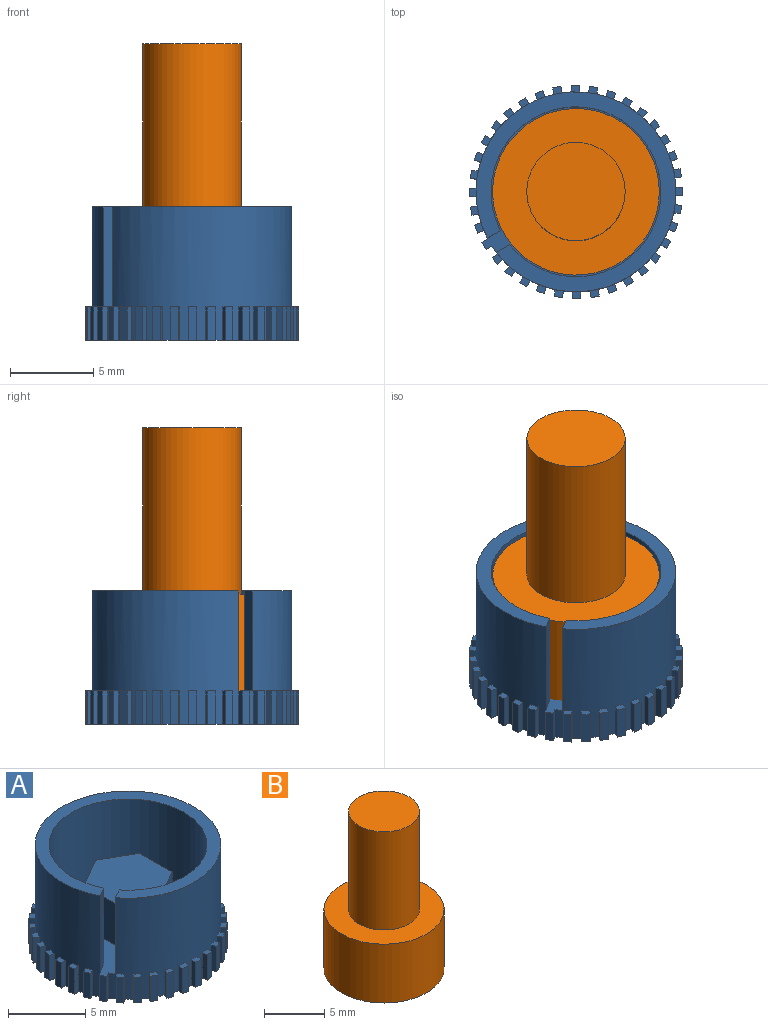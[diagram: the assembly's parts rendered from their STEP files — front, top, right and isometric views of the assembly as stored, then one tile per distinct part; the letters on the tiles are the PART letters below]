
ASSEMBLY  parts=2 mates=1
PART A: 157 faces, bbox 12.8x12.8x8 mm
  f0: plane 3.3x2.55mm, normal (-0.5,-0.87,0), area 9.7mm2, adj f1,f5,f6,f131
  f1: plane 3.3x2.94mm, normal (-1,0,0), area 9.7mm2, adj f0,f2,f6,f131
  f2: plane 3.3x2.55mm, normal (-0.5,0.86,0), area 9.7mm2, adj f1,f3,f6,f131
  f3: plane 3.3x2.55mm, normal (0.5,0.87,0), area 9.7mm2, adj f2,f4,f6,f131
  f4: plane 3.3x2.94mm, normal (1,0,0), area 9.7mm2, adj f3,f5,f6,f131
  f5: plane 3.3x2.55mm, normal (0.5,-0.86,0), area 9.7mm2, adj f0,f4,f6,f131
  f6: plane 5.89x5.11mm, normal (0,0,1), area 22.5mm2, adj f0,f1,f2,f3,f4,f5
  f7: cylinder r=5.1mm len=10.2mm, axis (0,0,-1), area 186.2mm2, adj f8,f131,f155,f156
  f8: plane 12x12mm, normal (0,0,1), area 30.5mm2, adj f7,f84,f155,f156
  f9: plane 12.79x12.79mm, normal (0,0,-1), area 120.2mm2, adj f10,f11,f12,f13,f14,f15,f16,f17
  f10: plane 2x0.47mm, normal (0.35,-0.94,0), area 1mm2, adj f9,f11,f153,f154
  f11: plane 2x0.38mm, normal (-0.94,-0.35,0), area 0.8mm2, adj f9,f10,f84,f154
  f12: plane 2x0.49mm, normal (0.18,-0.98,0), area 1mm2, adj f9,f150,f151,f152
  f13: plane 2x0.5mm, normal (0.01,-1,0), area 1mm2, adj f9,f147,f148,f149
  f14: plane 2x0.49mm, normal (-0.17,-0.99,0), area 1mm2, adj f9,f144,f145,f146
  f15: plane 2x0.47mm, normal (-0.34,-0.94,0), area 1mm2, adj f9,f141,f142,f143
  f16: plane 2x0.43mm, normal (-0.49,-0.87,0), area 1mm2, adj f9,f138,f139,f140
  f17: plane 2x0.39mm, normal (-0.64,-0.77,0), area 1mm2, adj f9,f135,f136,f137
  f18: plane 2x0.38mm, normal (-0.76,-0.65,0), area 1mm2, adj f9,f132,f133,f134
  f19: plane 2x0.43mm, normal (-0.86,-0.51,0), area 1mm2, adj f9,f129,f130,f131
  f20: plane 2x0.47mm, normal (-0.94,-0.35,0), area 1mm2, adj f9,f126,f127,f128
  f21: plane 2x0.49mm, normal (-0.98,-0.18,0), area 1mm2, adj f9,f123,f124,f125
  f22: plane 2x0.5mm, normal (-1,-0.01,0), area 1mm2, adj f9,f120,f121,f122
  f23: plane 2x0.49mm, normal (-0.99,0.17,0), area 1mm2, adj f9,f117,f118,f119
  f24: plane 2x0.47mm, normal (-0.94,0.34,0), area 1mm2, adj f9,f114,f115,f116
  f25: plane 2x0.43mm, normal (-0.87,0.49,0), area 1mm2, adj f9,f111,f112,f113
  f26: plane 2x0.39mm, normal (-0.77,0.64,0), area 1mm2, adj f9,f108,f109,f110
  f27: plane 2x0.38mm, normal (-0.65,0.76,0), area 1mm2, adj f9,f105,f106,f107
  f28: plane 2x0.43mm, normal (-0.51,0.86,0), area 1mm2, adj f9,f102,f103,f104
  f29: plane 2x0.47mm, normal (-0.35,0.94,0), area 1mm2, adj f9,f99,f100,f101
  f30: plane 2x0.49mm, normal (-0.18,0.98,0), area 1mm2, adj f9,f96,f97,f98
  f31: plane 2x0.5mm, normal (-0.01,1,0), area 1mm2, adj f9,f93,f94,f95
  f32: plane 2x0.49mm, normal (0.17,0.99,0), area 1mm2, adj f9,f90,f91,f92
  f33: plane 2x0.47mm, normal (0.34,0.94,0), area 1mm2, adj f9,f87,f88,f89
  f34: plane 2x0.43mm, normal (0.49,0.87,0), area 1mm2, adj f9,f83,f85,f86
  f35: plane 2x0.39mm, normal (0.64,0.77,0), area 1mm2, adj f9,f80,f81,f82
  f36: plane 2x0.38mm, normal (0.76,0.65,0), area 1mm2, adj f9,f77,f78,f79
  f37: plane 2x0.43mm, normal (0.86,0.51,0), area 1mm2, adj f9,f74,f75,f76
  f38: plane 2x0.47mm, normal (0.94,0.35,0), area 1mm2, adj f9,f71,f72,f73
  f39: plane 2x0.49mm, normal (0.98,0.18,0), area 1mm2, adj f9,f68,f69,f70
  f40: plane 2x0.5mm, normal (1,0.01,0), area 1mm2, adj f9,f65,f66,f67
  f41: plane 2x0.49mm, normal (0.99,-0.17,0), area 1mm2, adj f9,f62,f63,f64
  f42: plane 2x0.47mm, normal (0.94,-0.34,0), area 1mm2, adj f9,f59,f60,f61
  f43: plane 2x0.43mm, normal (0.87,-0.49,0), area 1mm2, adj f9,f56,f57,f58
  f44: plane 2x0.39mm, normal (0.77,-0.64,0), area 1mm2, adj f9,f53,f54,f55
  f45: plane 2x0.38mm, normal (0.65,-0.76,0), area 1mm2, adj f9,f50,f51,f52
  f46: plane 2x0.35mm, normal (0.86,0.51,0), area 0.8mm2, adj f9,f47,f49,f84
  f47: plane 2x0.43mm, normal (0.51,-0.86,0), area 1mm2, adj f9,f46,f48,f49
  f48: plane 2x0.35mm, normal (-0.86,-0.51,0), area 0.8mm2, adj f9,f47,f49,f84
  f49: plane 0.63x0.6mm, normal (0,0,1), area 0.2mm2, adj f46,f47,f48,f84
  f50: plane 2x0.3mm, normal (-0.76,-0.65,0), area 0.8mm2, adj f9,f45,f52,f84
  f51: plane 2x0.3mm, normal (0.76,0.65,0), area 0.8mm2, adj f9,f45,f52,f84
  f52: plane 0.64x0.63mm, normal (0,0,1), area 0.2mm2, adj f45,f50,f51,f84
  f53: plane 2x0.31mm, normal (-0.64,-0.77,0), area 0.8mm2, adj f9,f44,f55,f84
  f54: plane 2x0.31mm, normal (0.64,0.77,0), area 0.8mm2, adj f9,f44,f55,f84
  f55: plane 0.64x0.63mm, normal (0,0,1), area 0.2mm2, adj f44,f53,f54,f84
  f56: plane 2x0.35mm, normal (-0.49,-0.87,0), area 0.8mm2, adj f9,f43,f58,f84
  f57: plane 2x0.35mm, normal (0.49,0.87,0), area 0.8mm2, adj f9,f43,f58,f84
  f58: plane 0.63x0.6mm, normal (0,0,1), area 0.2mm2, adj f43,f56,f57,f84
  f59: plane 2x0.38mm, normal (-0.34,-0.94,0), area 0.8mm2, adj f9,f42,f61,f84
  f60: plane 2x0.38mm, normal (0.34,0.94,0), area 0.8mm2, adj f9,f42,f61,f84
  f61: plane 0.61x0.54mm, normal (0,0,1), area 0.2mm2, adj f42,f59,f60,f84
  f62: plane 2x0.39mm, normal (-0.17,-0.99,0), area 0.8mm2, adj f9,f41,f64,f84
  f63: plane 2x0.39mm, normal (0.17,0.99,0), area 0.8mm2, adj f9,f41,f64,f84
  f64: plane 0.56x0.48mm, normal (0,0,1), area 0.2mm2, adj f41,f62,f63,f84
  f65: plane 2x0.4mm, normal (0.01,-1,0), area 0.8mm2, adj f9,f40,f67,f84
  f66: plane 2x0.4mm, normal (-0.01,1,0), area 0.8mm2, adj f9,f40,f67,f84
  f67: plane 0.5x0.4mm, normal (0,0,1), area 0.2mm2, adj f40,f65,f66,f84
  f68: plane 2x0.39mm, normal (0.18,-0.98,0), area 0.8mm2, adj f9,f39,f70,f84
  f69: plane 2x0.39mm, normal (-0.18,0.98,0), area 0.8mm2, adj f9,f39,f70,f84
  f70: plane 0.56x0.48mm, normal (0,0,1), area 0.2mm2, adj f39,f68,f69,f84
  f71: plane 2x0.38mm, normal (0.35,-0.94,0), area 0.8mm2, adj f9,f38,f73,f84
  f72: plane 2x0.38mm, normal (-0.35,0.94,0), area 0.8mm2, adj f9,f38,f73,f84
  f73: plane 0.61x0.55mm, normal (0,0,1), area 0.2mm2, adj f38,f71,f72,f84
  f74: plane 2x0.35mm, normal (0.51,-0.86,0), area 0.8mm2, adj f9,f37,f76,f84
  f75: plane 2x0.35mm, normal (-0.51,0.86,0), area 0.8mm2, adj f9,f37,f76,f84
  f76: plane 0.63x0.6mm, normal (0,0,1), area 0.2mm2, adj f37,f74,f75,f84
  f77: plane 2x0.3mm, normal (0.65,-0.76,0), area 0.8mm2, adj f9,f36,f79,f84
  f78: plane 2x0.3mm, normal (-0.65,0.76,0), area 0.8mm2, adj f9,f36,f79,f84
  f79: plane 0.64x0.63mm, normal (0,0,1), area 0.2mm2, adj f36,f77,f78,f84
  f80: plane 2x0.31mm, normal (0.77,-0.64,0), area 0.8mm2, adj f9,f35,f82,f84
  f81: plane 2x0.31mm, normal (-0.77,0.64,0), area 0.8mm2, adj f9,f35,f82,f84
  f82: plane 0.64x0.63mm, normal (0,0,1), area 0.2mm2, adj f35,f80,f81,f84
  f83: plane 2x0.35mm, normal (0.87,-0.49,0), area 0.8mm2, adj f9,f34,f84,f86
  f84: cylinder r=6mm len=12mm, axis (0,0,1), area 259.6mm2, adj f8,f9,f11,f46,f48,f49,f50,f51
  f85: plane 2x0.35mm, normal (-0.87,0.49,0), area 0.8mm2, adj f9,f34,f84,f86
  f86: plane 0.63x0.6mm, normal (0,0,1), area 0.2mm2, adj f34,f83,f84,f85
  f87: plane 2x0.38mm, normal (0.94,-0.34,0), area 0.8mm2, adj f9,f33,f84,f89
  f88: plane 2x0.38mm, normal (-0.94,0.34,0), area 0.8mm2, adj f9,f33,f84,f89
  f89: plane 0.61x0.54mm, normal (0,0,1), area 0.2mm2, adj f33,f84,f87,f88
  f90: plane 2x0.39mm, normal (0.99,-0.17,0), area 0.8mm2, adj f9,f32,f84,f92
  f91: plane 2x0.39mm, normal (-0.99,0.17,0), area 0.8mm2, adj f9,f32,f84,f92
  f92: plane 0.56x0.48mm, normal (0,0,1), area 0.2mm2, adj f32,f84,f90,f91
  f93: plane 2x0.4mm, normal (1,0.01,0), area 0.8mm2, adj f9,f31,f84,f95
  f94: plane 2x0.4mm, normal (-1,-0.01,0), area 0.8mm2, adj f9,f31,f84,f95
  f95: plane 0.5x0.4mm, normal (0,0,1), area 0.2mm2, adj f31,f84,f93,f94
  f96: plane 2x0.39mm, normal (0.98,0.18,0), area 0.8mm2, adj f9,f30,f84,f98
  f97: plane 2x0.39mm, normal (-0.98,-0.18,0), area 0.8mm2, adj f9,f30,f84,f98
  f98: plane 0.56x0.48mm, normal (0,0,1), area 0.2mm2, adj f30,f84,f96,f97
  f99: plane 2x0.38mm, normal (0.94,0.35,0), area 0.8mm2, adj f9,f29,f84,f101
  f100: plane 2x0.38mm, normal (-0.94,-0.35,0), area 0.8mm2, adj f9,f29,f84,f101
  f101: plane 0.61x0.55mm, normal (0,0,1), area 0.2mm2, adj f29,f84,f99,f100
  f102: plane 2x0.35mm, normal (0.86,0.51,0), area 0.8mm2, adj f9,f28,f84,f104
  f103: plane 2x0.35mm, normal (-0.86,-0.51,0), area 0.8mm2, adj f9,f28,f84,f104
  f104: plane 0.63x0.6mm, normal (0,0,1), area 0.2mm2, adj f28,f84,f102,f103
  f105: plane 2x0.3mm, normal (0.76,0.65,0), area 0.8mm2, adj f9,f27,f84,f107
  f106: plane 2x0.3mm, normal (-0.76,-0.65,0), area 0.8mm2, adj f9,f27,f84,f107
  f107: plane 0.64x0.63mm, normal (0,0,1), area 0.2mm2, adj f27,f84,f105,f106
  f108: plane 2x0.31mm, normal (0.64,0.77,0), area 0.8mm2, adj f9,f26,f84,f110
  f109: plane 2x0.31mm, normal (-0.64,-0.77,0), area 0.8mm2, adj f9,f26,f84,f110
  f110: plane 0.64x0.63mm, normal (0,0,1), area 0.2mm2, adj f26,f84,f108,f109
  f111: plane 2x0.35mm, normal (0.49,0.87,0), area 0.8mm2, adj f9,f25,f84,f113
  f112: plane 2x0.35mm, normal (-0.49,-0.87,0), area 0.8mm2, adj f9,f25,f84,f113
  f113: plane 0.63x0.6mm, normal (0,0,1), area 0.2mm2, adj f25,f84,f111,f112
  f114: plane 2x0.38mm, normal (0.34,0.94,0), area 0.8mm2, adj f9,f24,f84,f116
  f115: plane 2x0.38mm, normal (-0.34,-0.94,0), area 0.8mm2, adj f9,f24,f84,f116
  f116: plane 0.61x0.54mm, normal (0,0,1), area 0.2mm2, adj f24,f84,f114,f115
  f117: plane 2x0.39mm, normal (0.17,0.99,0), area 0.8mm2, adj f9,f23,f84,f119
  f118: plane 2x0.39mm, normal (-0.17,-0.99,0), area 0.8mm2, adj f9,f23,f84,f119
  f119: plane 0.56x0.48mm, normal (0,0,1), area 0.2mm2, adj f23,f84,f117,f118
  f120: plane 2x0.4mm, normal (-0.01,1,0), area 0.8mm2, adj f9,f22,f84,f122
  f121: plane 2x0.4mm, normal (0.01,-1,0), area 0.8mm2, adj f9,f22,f84,f122
  f122: plane 0.5x0.4mm, normal (0,0,1), area 0.2mm2, adj f22,f84,f120,f121
  f123: plane 2x0.39mm, normal (-0.18,0.98,0), area 0.8mm2, adj f9,f21,f84,f125
  f124: plane 2x0.39mm, normal (0.18,-0.98,0), area 0.8mm2, adj f9,f21,f84,f125
  f125: plane 0.56x0.48mm, normal (0,0,1), area 0.2mm2, adj f21,f84,f123,f124
  f126: plane 2x0.38mm, normal (-0.35,0.94,0), area 0.8mm2, adj f9,f20,f84,f128
  f127: plane 2x0.38mm, normal (0.35,-0.94,0), area 0.8mm2, adj f9,f20,f84,f128
  f128: plane 0.61x0.55mm, normal (0,0,1), area 0.2mm2, adj f20,f84,f126,f127
  f129: plane 2x0.35mm, normal (-0.51,0.86,0), area 0.8mm2, adj f9,f19,f84,f131
  f130: plane 2x0.35mm, normal (0.51,-0.86,0), area 0.8mm2, adj f9,f19,f84,f131
  f131: plane 10.74x10.2mm, normal (0,0,1), area 60.3mm2, adj f0,f1,f2,f3,f4,f5,f7,f19
  f132: plane 2x0.3mm, normal (-0.65,0.76,0), area 0.8mm2, adj f9,f18,f84,f134
  f133: plane 2x0.3mm, normal (0.65,-0.76,0), area 0.8mm2, adj f9,f18,f84,f134
  f134: plane 0.64x0.63mm, normal (0,0,1), area 0.2mm2, adj f18,f84,f132,f133
  f135: plane 2x0.31mm, normal (-0.77,0.64,0), area 0.8mm2, adj f9,f17,f84,f137
  f136: plane 2x0.31mm, normal (0.77,-0.64,0), area 0.8mm2, adj f9,f17,f84,f137
  f137: plane 0.64x0.63mm, normal (0,0,1), area 0.2mm2, adj f17,f84,f135,f136
  f138: plane 2x0.35mm, normal (-0.87,0.49,0), area 0.8mm2, adj f9,f16,f84,f140
  f139: plane 2x0.35mm, normal (0.87,-0.49,0), area 0.8mm2, adj f9,f16,f84,f140
  f140: plane 0.63x0.6mm, normal (0,0,1), area 0.2mm2, adj f16,f84,f138,f139
  f141: plane 2x0.38mm, normal (-0.94,0.34,0), area 0.8mm2, adj f9,f15,f84,f143
  f142: plane 2x0.38mm, normal (0.94,-0.34,0), area 0.8mm2, adj f9,f15,f84,f143
  f143: plane 0.61x0.54mm, normal (0,0,1), area 0.2mm2, adj f15,f84,f141,f142
  f144: plane 2x0.39mm, normal (-0.99,0.17,0), area 0.8mm2, adj f9,f14,f84,f146
  f145: plane 2x0.39mm, normal (0.99,-0.17,0), area 0.8mm2, adj f9,f14,f84,f146
  f146: plane 0.56x0.48mm, normal (0,0,1), area 0.2mm2, adj f14,f84,f144,f145
  f147: plane 2x0.4mm, normal (-1,-0.01,0), area 0.8mm2, adj f9,f13,f84,f149
  f148: plane 2x0.4mm, normal (1,0.01,0), area 0.8mm2, adj f9,f13,f84,f149
  f149: plane 0.5x0.4mm, normal (0,0,1), area 0.2mm2, adj f13,f84,f147,f148
  f150: plane 2x0.39mm, normal (-0.98,-0.18,0), area 0.8mm2, adj f9,f12,f84,f152
  f151: plane 2x0.39mm, normal (0.98,0.18,0), area 0.8mm2, adj f9,f12,f84,f152
  f152: plane 0.56x0.48mm, normal (0,0,1), area 0.2mm2, adj f12,f84,f150,f151
  f153: plane 2x0.38mm, normal (0.94,0.35,0), area 0.8mm2, adj f9,f10,f84,f154
  f154: plane 0.61x0.55mm, normal (0,0,1), area 0.2mm2, adj f10,f11,f84,f153
  f155: plane 6x0.78mm, normal (0.51,-0.86,0), area 5.4mm2, adj f7,f8,f84,f131
  f156: plane 6x0.79mm, normal (-0.49,0.87,0), area 5.5mm2, adj f7,f8,f84,f131
PART B: 12 faces, bbox 10x10x16 mm
  f0: plane 10x10mm, normal (0,0,-1), area 56.9mm2, adj f1,f5,f6,f7,f8,f9,f10
  f1: cylinder r=5mm len=10mm, axis (0,0,-1), area 188.5mm2, adj f0,f2
  f2: plane 10x10mm, normal (0,0,1), area 51.2mm2, adj f1,f3
  f3: cylinder r=2.95mm len=10mm, axis (0,0,-1), area 185.4mm2, adj f2,f4
  f4: plane 5.9x5.9mm, normal (0,0,1), area 27.3mm2, adj f3
  f5: plane 3.5x2.5mm, normal (-0.5,-0.87,0), area 10.1mm2, adj f0,f6,f10,f11
  f6: plane 3.5x2.5mm, normal (0.5,-0.86,0), area 10.1mm2, adj f0,f5,f7,f11
  f7: plane 3.5x2.89mm, normal (1,0,0), area 10.1mm2, adj f0,f6,f8,f11
  f8: plane 3.5x2.5mm, normal (0.5,0.87,0), area 10.1mm2, adj f0,f7,f9,f11
  f9: plane 3.5x2.5mm, normal (-0.5,0.86,0), area 10.1mm2, adj f0,f8,f10,f11
  f10: plane 3.5x2.89mm, normal (-1,0,0), area 10.1mm2, adj f0,f5,f9,f11
  f11: plane 5.77x5.01mm, normal (0,0,-1), area 21.7mm2, adj f5,f6,f7,f8,f9,f10
PLACE A rot(axis=(-0.52,-0.54,0.66),0deg) t=(-6.26,17.54,12.56)mm
PLACE B rot(axis=(-0.52,-0.54,0.66),0deg) t=(-2.41,-6.62,5.76)mm
MATE fastened B.f3 <-> A.f84  axis (0,0,-1) through (-2.41,-6.62,9.26)mm
